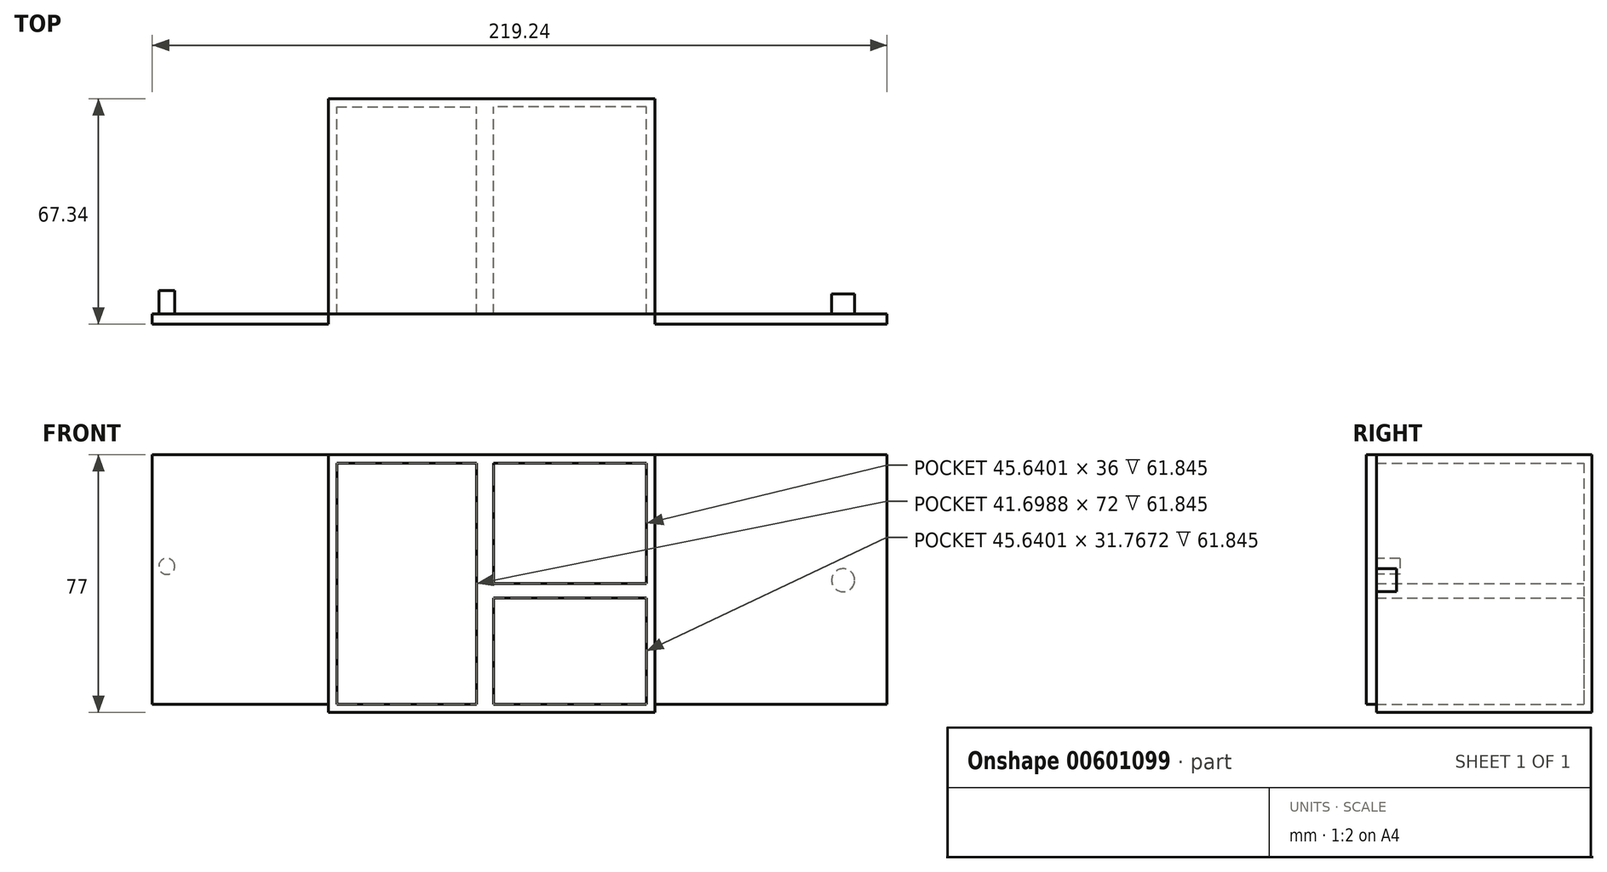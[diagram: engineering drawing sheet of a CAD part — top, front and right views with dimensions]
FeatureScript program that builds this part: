
annotation { "Feature Type Name" : "Feature", "Feature Type Description" : "" }
export const myFeature = defineFeature(function(context is Context, id is Id, definition is map)
    precondition{}
    {
        {
            var Q0;
            Q0=qCreatedBy(makeId("Top.planeOp"),FACE);
            var sketch = newSketch(context, id + "F0", { "sketchPlane" : qUnion([Q0])});
            skLineSegment(sketch, "E0.bottom", {"start": v(-46.8, -28.08) * mm, "end": v(45.64, -28.08) * mm});
            skLineSegment(sketch, "E0.top", {"start": v(-46.8, 33.76) * mm, "end": v(45.64, 33.76) * mm});
            skLineSegment(sketch, "E0.left", {"start": v(-46.8, -28.08) * mm, "end": v(-46.8, 33.76) * mm});
            skLineSegment(sketch, "E0.right", {"start": v(45.64, -28.08) * mm, "end": v(45.64, 33.76) * mm});
            skSolve(sketch);
        }
        {
            var Q0;
            Q0=makeQuery(id+"F0.imprint","IMPRINT",FACE,{"disambiguationData":[TD([[makeQuery(id+"F0.imprint","IMPRINT",EDGE,{"derivedFrom":sQuery(id+"F0.wireOp",EDGE,"E0.bottom")}),1.0]])]});
            extrude(context, id + "F1", {"entities" : qUnion([Q0]), "depth" : 72 * mm});
        }
        {
            var Q0;
            Q0=makeQuery(id+"F1.opExtrude","SWEPT_FACE",FACE,{"disambiguationData":[OSD([sQuery(id+"F0.wireOp",EDGE,"E0.bottom")])]});
            shell(context, id + "F2", {"entities" : qUnion([Q0]), "thickness" : 2.5 * mm, "oppositeDirection" : true});
        }
        {
            var Q0;
            {var subQ0=sQuery(id+"F0.wireOp",EDGE,"E0.right");var subQ1=sQuery(id+"F0.wireOp",EDGE,"E0.left");var subQ2=sQuery(id+"F0.wireOp",EDGE,"E0.top");var subQ3=sQuery(id+"F0.wireOp",EDGE,"E0.bottom");Q0=makeQuery(id+"F2.opShell","OFFSET_FACE",FACE,{"disambiguationData":[OSD([subQ3,subQ2,subQ1,subQ0]),TDD([makeQuery(id+"F1.opExtrude","CAP_FACE",FACE,{"disambiguationData":[OSD([subQ3,subQ2,subQ1,subQ0])],"isStart":true})])]});}
            var sketch = newSketch(context, id + "F3", { "sketchPlane" : qUnion([Q0])});
            skLineSegment(sketch, "E1.bottom", {"start": v(0, -28.08) * mm, "end": v(-5.1, -28.08) * mm});
            skLineSegment(sketch, "E1.top", {"start": v(0, 33.76) * mm, "end": v(-5.1, 33.76) * mm});
            skLineSegment(sketch, "E1.left", {"start": v(0, -28.08) * mm, "end": v(0, 33.76) * mm});
            skLineSegment(sketch, "E1.right", {"start": v(-5.1, -28.08) * mm, "end": v(-5.1, 33.76) * mm});
            skSolve(sketch);
        }
        {
            var Q0;
            Q0=qSketchRegion(id+"F3",true);
            extrude(context, id + "F4", {"entities" : qUnion([Q0]), "operationType" : NewBodyOperationType.ADD, "depth" : 72 * mm});
        }
        {
            var Q0;
            Q0=makeQuery(id+"F4.opExtrude","SWEPT_FACE",FACE,{"disambiguationData":[OSD([sQuery(id+"F3.wireOp",EDGE,"E1.left")])]});
            var sketch = newSketch(context, id + "F5", { "sketchPlane" : qUnion([Q0])});
            skLineSegment(sketch, "E2.bottom", {"start": v(-28.08, 36) * mm, "end": v(33.76, 36) * mm});
            skLineSegment(sketch, "E2.top", {"start": v(-28.08, 31.77) * mm, "end": v(33.76, 31.77) * mm});
            skLineSegment(sketch, "E2.left", {"start": v(-28.08, 36) * mm, "end": v(-28.08, 31.77) * mm});
            skLineSegment(sketch, "E2.right", {"start": v(33.76, 36) * mm, "end": v(33.76, 31.77) * mm});
            skSolve(sketch);
        }
        {
            var Q0;
            Q0=qSketchRegion(id+"F5",true);
            extrude(context, id + "F6", {"entities" : qUnion([Q0]), "operationType" : NewBodyOperationType.ADD, "depth" : 47 * mm});
        }
        {
            var Q0;
            Q0=makeQuery(id+"F6.boolean.opBoolean","MERGE",FACE,{"derivedFrom":[makeQuery(id+"F4.boolean.opBoolean","MERGE",FACE,{"derivedFrom":[makeQuery(id+"F1.opExtrude","SWEPT_FACE",FACE,{"disambiguationData":[OSD([sQuery(id+"F0.wireOp",EDGE,"E0.bottom")])]}),makeQuery(id+"F4.opExtrude","SWEPT_FACE",FACE,{"disambiguationData":[OSD([sQuery(id+"F3.wireOp",EDGE,"E1.bottom")])]})]}),makeQuery(id+"F6.opExtrude","SWEPT_FACE",FACE,{"disambiguationData":[OSD([sQuery(id+"F5.wireOp",EDGE,"E2.left")])]})]});
            var sketch = newSketch(context, id + "F7", { "sketchPlane" : qUnion([Q0])});
            skLineSegment(sketch, "E3.bottom", {"start": v(-49.3, 74.5) * mm, "end": v(-101.84, 74.5) * mm});
            skLineSegment(sketch, "E3.top", {"start": v(-49.3, 0) * mm, "end": v(-101.84, 0) * mm});
            skLineSegment(sketch, "E3.left", {"start": v(-49.3, 74.5) * mm, "end": v(-49.3, 0) * mm});
            skLineSegment(sketch, "E3.right", {"start": v(-101.84, 74.5) * mm, "end": v(-101.84, 0) * mm});
            skSolve(sketch);
        }
        {
            var Q0;
            Q0=makeQuery(id+"F7.imprint","IMPRINT",FACE,{"disambiguationData":[TD([[makeQuery(id+"F7.imprint","IMPRINT",EDGE,{"derivedFrom":sQuery(id+"F7.wireOp",EDGE,"E3.bottom")}),1.0]])]});
            extrude(context, id + "F8", {"entities" : qUnion([Q0]), "depth" : 3 * mm});
        }
        {
            var Q0;
            Q0=makeQuery(id+"F8.opExtrude","CAP_FACE",FACE,{"disambiguationData":[OSD([sQuery(id+"F7.wireOp",EDGE,"E3.bottom"),sQuery(id+"F7.wireOp",EDGE,"E3.top"),sQuery(id+"F7.wireOp",EDGE,"E3.left"),sQuery(id+"F7.wireOp",EDGE,"E3.right")])],"isStart":true});
            var sketch = newSketch(context, id + "F9", { "sketchPlane" : qUnion([Q0])});
            skCircle(sketch, "E4", {"center": v(97.5, 41.15) * mm, "radius": 2.39 * mm});
            skSolve(sketch);
        }
        {
            var Q0;
            Q0=qSketchRegion(id+"F9",true);
            extrude(context, id + "F10", {"entities" : qUnion([Q0]), "operationType" : NewBodyOperationType.ADD, "depth" : 7 * mm});
        }
        {
            var Q0;
            Q0=makeQuery(id+"F6.boolean.opBoolean","MERGE",FACE,{"derivedFrom":[makeQuery(id+"F4.boolean.opBoolean","MERGE",FACE,{"derivedFrom":[makeQuery(id+"F1.opExtrude","SWEPT_FACE",FACE,{"disambiguationData":[OSD([sQuery(id+"F0.wireOp",EDGE,"E0.bottom")])]}),makeQuery(id+"F4.opExtrude","SWEPT_FACE",FACE,{"disambiguationData":[OSD([sQuery(id+"F3.wireOp",EDGE,"E1.bottom")])]})]}),makeQuery(id+"F6.opExtrude","SWEPT_FACE",FACE,{"disambiguationData":[OSD([sQuery(id+"F5.wireOp",EDGE,"E2.left")])]})]});
            var sketch = newSketch(context, id + "F11", { "sketchPlane" : qUnion([Q0])});
            skLineSegment(sketch, "E5.bottom", {"start": v(48.14, 74.5) * mm, "end": v(117.4, 74.5) * mm});
            skLineSegment(sketch, "E5.top", {"start": v(48.14, 0) * mm, "end": v(117.4, 0) * mm});
            skLineSegment(sketch, "E5.left", {"start": v(48.14, 74.5) * mm, "end": v(48.14, 0) * mm});
            skLineSegment(sketch, "E5.right", {"start": v(117.4, 74.5) * mm, "end": v(117.4, 0) * mm});
            skSolve(sketch);
        }
        {
            var Q0;
            Q0=qSketchRegion(id+"F11",true);
            extrude(context, id + "F12", {"entities" : qUnion([Q0]), "depth" : 3 * mm});
        }
        {
            var Q0;
            Q0=makeQuery(id+"F12.opExtrude","CAP_FACE",FACE,{"disambiguationData":[OSD([sQuery(id+"F11.wireOp",EDGE,"E5.bottom"),sQuery(id+"F11.wireOp",EDGE,"E5.top"),sQuery(id+"F11.wireOp",EDGE,"E5.left"),sQuery(id+"F11.wireOp",EDGE,"E5.right")])],"isStart":true});
            var sketch = newSketch(context, id + "F13", { "sketchPlane" : qUnion([Q0])});
            skCircle(sketch, "E6", {"center": v(-104.3, 37) * mm, "radius": 3.45 * mm});
            skSolve(sketch);
        }
        {
            var Q0;
            Q0=makeQuery(id+"F13.imprint","IMPRINT",FACE,{"disambiguationData":[TD([[makeQuery(id+"F13.imprint","IMPRINT",EDGE,{"derivedFrom":sQuery(id+"F13.wireOp",EDGE,"E6")}),1.0]])]});
            extrude(context, id + "F14", {"entities" : qUnion([Q0]), "operationType" : NewBodyOperationType.ADD, "depth" : 6 * mm});
        }
    });
